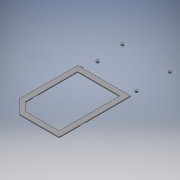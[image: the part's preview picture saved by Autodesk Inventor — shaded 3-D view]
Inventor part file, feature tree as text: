
AUTODESK INVENTOR PART (.ipt)
format: ipt  version: 2016 SP2 (Build 200236200, 236)  size: 161,280 bytes
history: native  units: mm
features: reference x19, extrude x3, sketch x3
ambient origin geometry x8: Origin, YZ Plane, XZ Plane, XY Plane, X Axis, Y Axis, Z Axis, Center Point
bodies: Volumenkörper1 (feature_tree)
feature tree (25):
  extrude  "Extrusion1"  Depth=8.0mm
  extrude  "Extrusion2"  Depth=10.0mm
  extrude  "Extrusion3"  Depth=10.0mm
  sketch  "Skizze1"  dims[d0=135.0deg d1=8.0mm]
  reference  "Referenz1"
  reference  "Referenz2"
  reference  "Referenz3"
  reference  "Referenz4"
  reference  "Referenz6"
  reference  "Referenz7"
  reference  "Referenz8"
  reference  "Referenz9"
  reference  "Referenz10"
  reference  "Referenz11"
  reference  "Referenz12"
  reference  "Referenz13"
  reference  "Referenz14"
  sketch  "Skizze2"  dims[d3=10.0mm d4=10.0mm]
  sketch  "Skizze3"  dims[d5=10.0mm d6=10.0mm d7=1.5mm d8=0.0mm d9=2.6mm d10=0.0mm d11=10.0mm d12=10.0mm d13=10.0mm d14=0.0mm d15=40.0mm d16=2.0mm d17=1.0mm d18=0.0mm d22=2.5mm d23=0.1mm d24=4.8mm d25=4.8mm d26=4.8mm d27=4.8mm d28=4.8mm d29=4.8mm]
  reference  "Referenz21"
  reference  "Referenz22"
  reference  "Referenz23"
  reference  "Referenz24"
  reference  "Referenz25"
  reference  "Referenz26"
